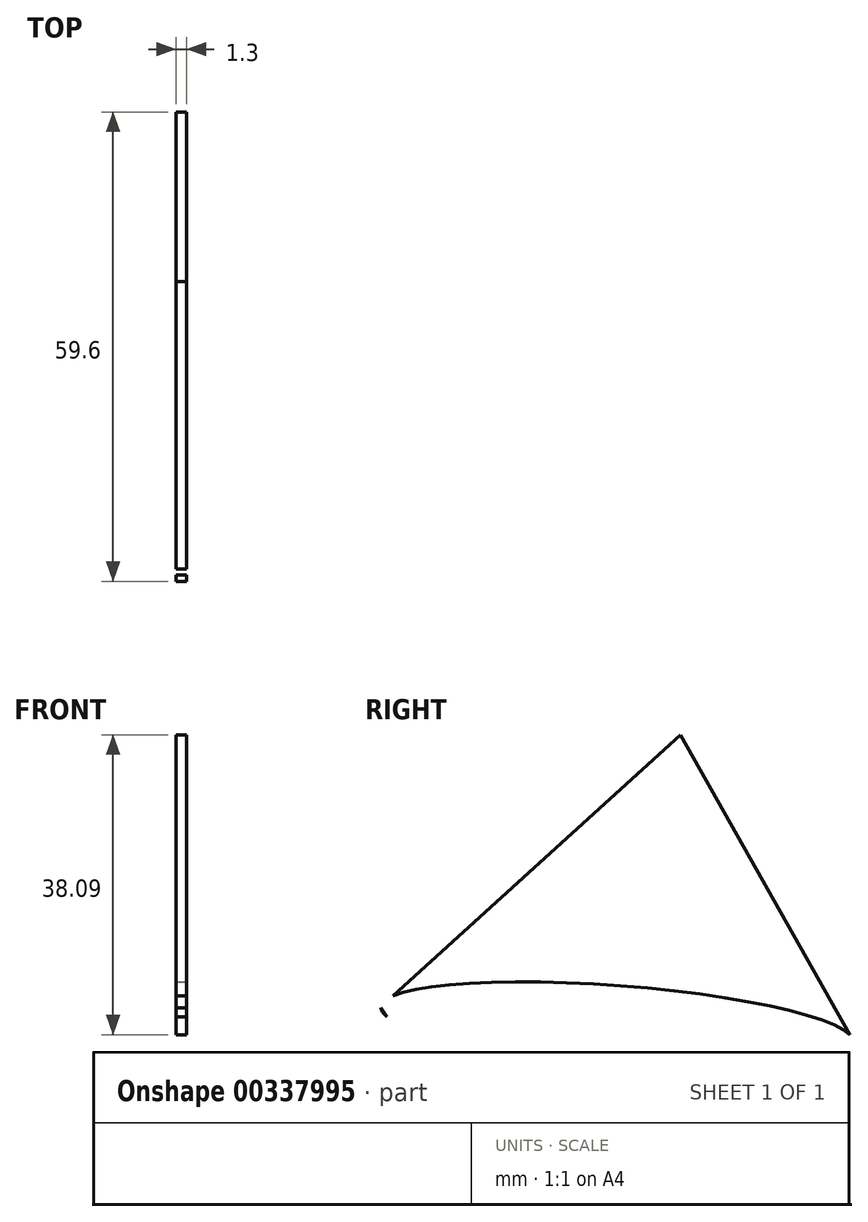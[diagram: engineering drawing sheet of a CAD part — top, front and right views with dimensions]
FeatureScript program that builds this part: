
annotation { "Feature Type Name" : "Feature", "Feature Type Description" : "" }
export const myFeature = defineFeature(function(context is Context, id is Id, definition is map)
    precondition{}
    {
        {
            var Q0;
            Q0=qCreatedBy(makeId("Right.planeOp"),FACE);
            var sketch = newSketch(context, id + "F0", { "sketchPlane" : qUnion([Q0])});
            skEllipse(sketch, "E0", {"center": v(0, 9.91) * mm, "majorRadius": 30.13 * mm, "minorRadius": 4.97 * mm, "majorAxis": v(-1, 0.08)});
            skLineSegment(sketch, "E1", {"start": v(-30.05, 12.06) * mm, "end": v(-5.2, -23.51) * mm});
            skPoint(sketch, "E1.startSnap0", {"position": v(-30.05, 12.18) * mm});
            skLineSegment(sketch, "E2", {"start": v(30.05, 7.77) * mm, "end": v(-5.2, -23.51) * mm});
            skPoint(sketch, "E2.startSnap0", {"position": v(30.05, 7.65) * mm});
            skLineSegment(sketch, "E3", {"start": v(-30.05, 12.18) * mm, "end": v(8.01, 46.74) * mm});
            skLineSegment(sketch, "E4", {"start": v(8.01, 46.74) * mm, "end": v(30.05, 7.77) * mm});
            skSolve(sketch);
        }
        {
            var Q0;
            {var subQ0=sQuery(id+"F0.wireOp",EDGE,"E4");var subQ1=sQuery(id+"F0.wireOp",EDGE,"E0");var subQ2=makeQuery(id+"F0.imprint","INTERSECT",VERTEX,{"derivedFrom":[subQ1,subQ0]});Q0=makeQuery(id+"F0.imprint","IMPRINT",FACE,{"disambiguationData":[TD([[makeQuery(id+"F0.imprint","IMPRINT",EDGE,{"disambiguationData":[TD([[subQ2,-1.0]])],"derivedFrom":subQ1}),-1.0]])]});}
            var Q1;
            {var subQ0=sQuery(id+"F0.wireOp",EDGE,"E1");var subQ1=sQuery(id+"F0.wireOp",EDGE,"E0");var subQ2=makeQuery(id+"F0.imprint","INTERSECT",VERTEX,{"disambiguationData":[OD(1.0)],"derivedFrom":[subQ1,subQ0]});Q1=makeQuery(id+"F0.imprint","IMPRINT",FACE,{"disambiguationData":[TD([[makeQuery(id+"F0.imprint","IMPRINT",EDGE,{"disambiguationData":[TD([[subQ2,-1.0]])],"derivedFrom":subQ1}),-1.0]])]});}
            var Q2;
            {var subQ0=sQuery(id+"F0.wireOp",EDGE,"E1");var subQ1=sQuery(id+"F0.wireOp",EDGE,"E0");var subQ2=makeQuery(id+"F0.imprint","INTERSECT",VERTEX,{"disambiguationData":[OD(0.0)],"derivedFrom":[subQ1,subQ0]});Q2=makeQuery(id+"F0.imprint","IMPRINT",FACE,{"disambiguationData":[TD([[makeQuery(id+"F0.imprint","IMPRINT",EDGE,{"disambiguationData":[TD([[subQ2,1.0]])],"derivedFrom":subQ1}),1.0]])]});}
            extrude(context, id + "F1", {"entities" : qUnion([Q0, Q1, Q2]), "depth" : 1.3 * mm});
        }
    });
